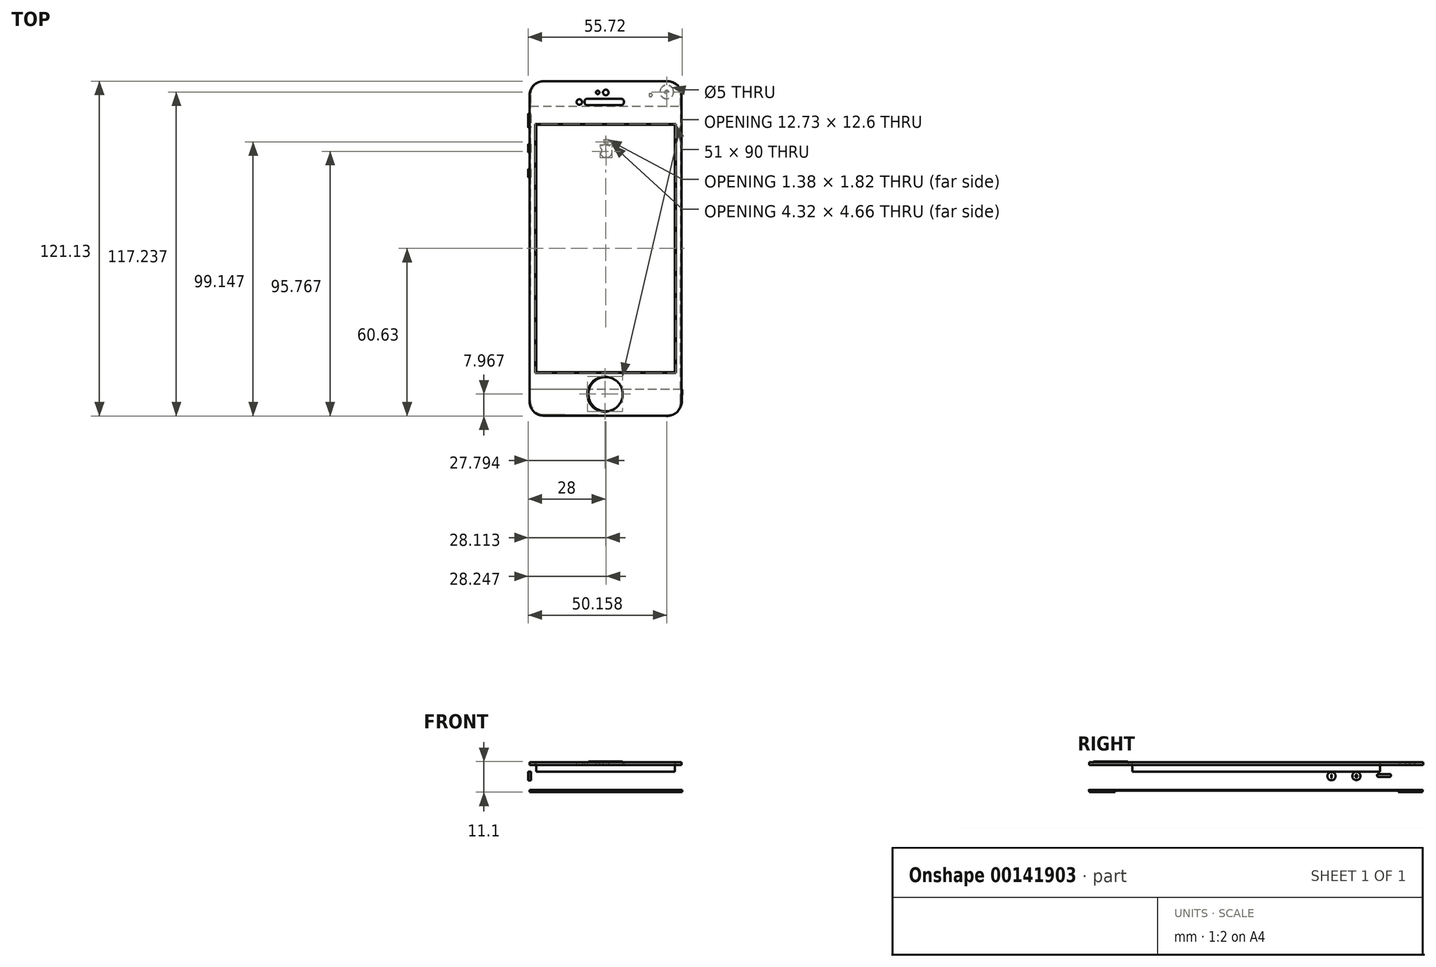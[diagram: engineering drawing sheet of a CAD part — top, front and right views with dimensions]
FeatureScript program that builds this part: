
annotation { "Feature Type Name" : "Feature", "Feature Type Description" : "" }
export const myFeature = defineFeature(function(context is Context, id is Id, definition is map)
    precondition{}
    {
        {
            assignVariable(context, id + "F0", {"name" : "depthofphone", "anyValue" : 1});
        }
        {
            var Q0;
            Q0=qCreatedBy(makeId("Top.planeOp"),FACE);
            var sketch = newSketch(context, id + "F1", { "sketchPlane" : qUnion([Q0])});
            skLineSegment(sketch, "E0.bottom", {"start": v(25.5, 45) * mm, "end": v(-25.5, 45) * mm});
            skLineSegment(sketch, "E0.top", {"start": v(25.5, -45) * mm, "end": v(-25.5, -45) * mm});
            skLineSegment(sketch, "E0.left", {"start": v(25.5, 45) * mm, "end": v(25.5, -45) * mm});
            skLineSegment(sketch, "E0.right", {"start": v(-25.5, 45) * mm, "end": v(-25.5, -45) * mm});
            skPoint(sketch, "E0.middle", {"position": v(0, 0) * mm});
            skLineSegment(sketch, "E1.bottom", {"start": v(22.5, 60.5) * mm, "end": v(-22.5, 60.5) * mm});
            skLineSegment(sketch, "E1.top", {"start": v(22.5, -60.5) * mm, "end": v(-22.5, -60.5) * mm});
            skLineSegment(sketch, "E1.left", {"start": v(27.5, 55.5) * mm, "end": v(27.5, -55.5) * mm});
            skLineSegment(sketch, "E1.right", {"start": v(-27.5, 55.5) * mm, "end": v(-27.5, -55.5) * mm});
            skPoint(sketch, "E2.visualSharp", {"position": v(-27.5, 60.5) * mm});
            skArc(sketch, "E2.filletArc", {"start": v(-22.5, 60.5) * mm, "mid": v(-26.04, 59.04) * mm, "end": v(-27.5, 55.5) * mm});
            skPoint(sketch, "E3.visualSharp", {"position": v(27.5, 60.5) * mm});
            skArc(sketch, "E3.filletArc", {"start": v(27.5, 55.5) * mm, "mid": v(26.04, 59.04) * mm, "end": v(22.5, 60.5) * mm});
            skPoint(sketch, "E4.visualSharp", {"position": v(-27.5, -60.5) * mm});
            skArc(sketch, "E4.filletArc", {"start": v(-27.5, -55.5) * mm, "mid": v(-26.04, -59.04) * mm, "end": v(-22.5, -60.5) * mm});
            skPoint(sketch, "E5.visualSharp", {"position": v(27.5, -60.5) * mm});
            skArc(sketch, "E5.filletArc", {"start": v(22.5, -60.5) * mm, "mid": v(26.04, -59.04) * mm, "end": v(27.5, -55.5) * mm});
            skSolve(sketch);
        }
        {
            var Q0;
            Q0=qCreatedBy(makeId("Top.planeOp"),FACE);
            cPlane(context, id + "F2", {"entities" : qUnion([Q0]), "cplaneType" : CPlaneType.OFFSET, "offset" : 2 * mm, "width" : 150 * mm, "height" : 150 * mm});
        }
        {
            var Q0;
            Q0=qCreatedBy(id+"F2.planeOp",FACE);
            var sketch = newSketch(context, id + "F3", { "sketchPlane" : qUnion([Q0])});
            skLineSegment(sketch, "E6", {"start": v(-6.75, 52) * mm, "end": v(5.75, 52) * mm});
            skLineSegment(sketch, "E7", {"start": v(6.5, 52.75) * mm, "end": v(6.5, 53.25) * mm});
            skLineSegment(sketch, "E8", {"start": v(5.75, 54) * mm, "end": v(-6.75, 54) * mm});
            skLineSegment(sketch, "E9", {"start": v(-7.5, 53.25) * mm, "end": v(-7.5, 52.75) * mm});
            skPoint(sketch, "E10.visualSharp", {"position": v(-7.5, 54) * mm});
            skArc(sketch, "E10.filletArc", {"start": v(-6.75, 54) * mm, "mid": v(-7.28, 53.78) * mm, "end": v(-7.5, 53.25) * mm});
            skPoint(sketch, "E11.visualSharp", {"position": v(-7.5, 52) * mm});
            skArc(sketch, "E11.filletArc", {"start": v(-7.5, 52.75) * mm, "mid": v(-7.28, 52.22) * mm, "end": v(-6.75, 52) * mm});
            skPoint(sketch, "E12.visualSharp", {"position": v(6.5, 52) * mm});
            skArc(sketch, "E12.filletArc", {"start": v(5.75, 52) * mm, "mid": v(6.28, 52.22) * mm, "end": v(6.5, 52.75) * mm});
            skPoint(sketch, "E13.visualSharp", {"position": v(6.5, 54) * mm});
            skArc(sketch, "E13.filletArc", {"start": v(6.5, 53.25) * mm, "mid": v(6.28, 53.78) * mm, "end": v(5.75, 54) * mm});
            skCircle(sketch, "E14", {"center": v(-9.5, 52.96) * mm, "radius": 0.9 * mm});
            skCircle(sketch, "E15", {"center": v(0.08, 56.42) * mm, "radius": 0.92 * mm});
            skCircle(sketch, "E16", {"center": v(-2.85, 56.45) * mm, "radius": 0.51 * mm});
            skCircle(sketch, "E17", {"center": v(-0.25, -52.75) * mm, "radius": 6.25 * mm});
            skSolve(sketch);
        }
        {
            var Q0;
            Q0 = qSketchRegion(id + "F1", true);
            extrude(context, id + "F4", {"entities" : qUnion([Q0]), "oppositeDirection" : true, "depth" : (getVariable(context, 'depthofphone')) * mm});
        }
        {
            var Q0;
            Q0 = qSketchRegion(id + "F3", true);
            extrude(context, id + "F5", {"entities" : qUnion([Q0]), "operationType" : NewBodyOperationType.REMOVE, "oppositeDirection" : true, "depth" : 3.74 * mm, "hasDraft" : true, "draftAngle" : 3 * degree});
        }
        {
            var Q0;
            Q0=qCreatedBy(makeId("Top.planeOp"),FACE);
            cPlane(context, id + "F6", {"entities" : qUnion([Q0]), "cplaneType" : CPlaneType.OFFSET, "offset" : 0.1 * mm, "oppositeDirection" : true, "width" : 150 * mm, "height" : 150 * mm});
        }
        {
            var Q0;
            Q0=qCreatedBy(id+"F6.planeOp",FACE);
            var sketch = newSketch(context, id + "F7", { "sketchPlane" : qUnion([Q0])});
            skLineSegment(sketch, "E18.bottom", {"start": v(25.05, 44.77) * mm, "end": v(-25.05, 44.77) * mm});
            skLineSegment(sketch, "E18.top", {"start": v(25.05, -44.77) * mm, "end": v(-25.05, -44.77) * mm});
            skLineSegment(sketch, "E18.left", {"start": v(25.05, 44.77) * mm, "end": v(25.05, -44.77) * mm});
            skLineSegment(sketch, "E18.right", {"start": v(-25.05, 44.77) * mm, "end": v(-25.05, -44.77) * mm});
            skPoint(sketch, "E18.middle", {"position": v(0, 0) * mm});
            skSolve(sketch);
        }
        {
            var Q0;
            Q0 = qSketchRegion(id + "F7", true);
            extrude(context, id + "F8", {"entities" : qUnion([Q0]), "oppositeDirection" : true, "depth" : 3.38 * mm});
        }
        {
            var Q0;
            Q0=qCreatedBy(id+"F6.planeOp",FACE);
            cPlane(context, id + "F9", {"entities" : qUnion([Q0]), "cplaneType" : CPlaneType.OFFSET, "offset" : 10 * mm, "oppositeDirection" : true, "width" : 150 * mm, "height" : 150 * mm});
        }
        {
            var Q0;
            Q0=qCreatedBy(id+"F9.planeOp",FACE);
            var sketch = newSketch(context, id + "F10", { "sketchPlane" : qUnion([Q0])});
            skLineSegment(sketch, "E19.left", {"start": v(27.13, -55.64) * mm, "end": v(27.22, 55.3) * mm});
            skLineSegment(sketch, "E19.right", {"start": v(-27.22, -55.1) * mm, "end": v(-27.13, 55.53) * mm});
            skPoint(sketch, "E19.middle", {"position": v(0, 0) * mm});
            skLineSegment(sketch, "E20", {"start": v(1.17, 33.01) * mm, "end": v(0.88, 32.83) * mm});
            skFitSpline(sketch, "E21", {"points": [v(-0.8, 33.02) * mm, v(-1.91, 34.28) * mm], "startDerivative": vector(-0.77, 0.53) * mm, "endDerivative": vector(-0.16, 0.9) * mm});
            skArc(sketch, "E22", {"start": v(1.17, 33.01) * mm, "mid": v(2.4, 35.13) * mm, "end": v(1.16, 37.25) * mm});
            skFitSpline(sketch, "E23", {"points": [v(1.16, 37.25) * mm, v(0.96, 37.34) * mm, v(0.74, 37.34) * mm, v(0.5, 37.25) * mm, v(0.3, 37.4) * mm, v(-0.28, 37.46) * mm, v(-1.27, 37.25) * mm, v(-1.91, 36.38) * mm], "startDerivative": vector(-2.14, 1.37) * mm, "endDerivative": vector(-2.3, -4.96) * mm});
            skFitSpline(sketch, "E24", {"points": [v(0.88, 32.83) * mm, v(0.59, 32.83) * mm, v(0.35, 33.06) * mm, v(-0.02, 33.08) * mm, v(-0.23, 32.83) * mm, v(-0.8, 33.02) * mm], "startDerivative": vector(-1.8, -0.36) * mm, "endDerivative": vector(-2.64, 1.48) * mm});
            skArc(sketch, "E25", {"start": v(-1.91, 36.38) * mm, "mid": v(-1.32, 35.33) * mm, "end": v(-1.91, 34.28) * mm});
            skFitSpline(sketch, "E26", {"points": [v(0.75, 37.6) * mm, v(-0.23, 38.24) * mm, v(-0.49, 39.44) * mm, v(0.49, 38.65) * mm, v(0.8, 37.99) * mm, v(0.75, 37.6) * mm]});
            skPoint(sketch, "E27.visualSharp", {"position": v(-27.22, -65.5) * mm});
            skPoint(sketch, "E28.visualSharp", {"position": v(27.12, -66.16) * mm});
            skPoint(sketch, "E29.visualSharp", {"position": v(-27.12, 66.16) * mm});
            skLineSegment(sketch, "E30", {"start": v(22.2, 60.3) * mm, "end": v(-22.42, 60.2) * mm});
            skLineSegment(sketch, "E31", {"start": v(22.07, -60.63) * mm, "end": v(-22.27, -60.1) * mm});
            skPoint(sketch, "E32.visualSharp", {"position": v(27.13, -60.7) * mm});
            skArc(sketch, "E32.filletArc", {"start": v(22.07, -60.63) * mm, "mid": v(25.65, -59.19) * mm, "end": v(27.13, -55.64) * mm});
            skPoint(sketch, "E33.visualSharp", {"position": v(-27.22, -60.05) * mm});
            skArc(sketch, "E33.filletArc", {"start": v(-27.22, -55.1) * mm, "mid": v(-25.77, -58.62) * mm, "end": v(-22.27, -60.1) * mm});
            skPoint(sketch, "E34.visualSharp", {"position": v(27.22, 60.3) * mm});
            skArc(sketch, "E34.filletArc", {"start": v(27.22, 55.3) * mm, "mid": v(25.75, 58.84) * mm, "end": v(22.2, 60.3) * mm});
            skPoint(sketch, "E35.visualSharp", {"position": v(-27.13, 60.2) * mm});
            skLineSegment(sketch, "E36", {"start": v(-25.9, 58.82) * mm, "end": v(-26.18, 58.5) * mm});
            skPoint(sketch, "E37.visualSharp", {"position": v(-27.13, 57.4) * mm});
            skArc(sketch, "E37.filletArc", {"start": v(-25.9, 58.82) * mm, "mid": v(-26.81, 57.29) * mm, "end": v(-27.13, 55.53) * mm});
            skPoint(sketch, "E38.visualSharp", {"position": v(-24.69, 60.2) * mm});
            skArc(sketch, "E38.filletArc", {"start": v(-22.42, 60.2) * mm, "mid": v(-24.49, 59.76) * mm, "end": v(-26.18, 58.5) * mm});
            skSolve(sketch);
        }
        {
            var Q0;
            Q0 = qSketchRegion(id + "F10", true);
            extrude(context, id + "F11", {"entities" : qUnion([Q0]), "oppositeDirection" : true, "depth" : 0.25 * mm});
        }
        {
            var Q0;
            Q0=qCreatedBy(id+"F9.planeOp",FACE);
            var sketch = newSketch(context, id + "F12", { "sketchPlane" : qUnion([Q0])});
            skLineSegment(sketch, "E39", {"start": v(-27.17, 51.46) * mm, "end": v(27.1, 51.46) * mm});
            skLineSegment(sketch, "E40", {"start": v(27.1, 51.46) * mm, "end": v(27.1, 55.4) * mm});
            skLineSegment(sketch, "E41", {"start": v(25.88, 58.7) * mm, "end": v(25.72, 58.87) * mm});
            skLineSegment(sketch, "E42", {"start": v(22.28, 60.23) * mm, "end": v(-22.4, 60.23) * mm});
            skLineSegment(sketch, "E43", {"start": v(-25.58, 59.1) * mm, "end": v(-25.85, 58.84) * mm});
            skLineSegment(sketch, "E44", {"start": v(-27.12, 55.56) * mm, "end": v(-27.17, 51.46) * mm});
            skPoint(sketch, "E45.visualSharp", {"position": v(-27.1, 57.66) * mm});
            skArc(sketch, "E45.filletArc", {"start": v(-25.58, 59.1) * mm, "mid": v(-26.7, 57.49) * mm, "end": v(-27.12, 55.56) * mm});
            skPoint(sketch, "E46.visualSharp", {"position": v(-24.4, 60.23) * mm});
            skArc(sketch, "E46.filletArc", {"start": v(-22.4, 60.23) * mm, "mid": v(-24.26, 59.87) * mm, "end": v(-25.85, 58.84) * mm});
            skPoint(sketch, "E47.visualSharp", {"position": v(24.4, 60.23) * mm});
            skArc(sketch, "E47.filletArc", {"start": v(25.88, 58.7) * mm, "mid": v(24.24, 59.83) * mm, "end": v(22.28, 60.23) * mm});
            skPoint(sketch, "E48.visualSharp", {"position": v(27.1, 57.41) * mm});
            skArc(sketch, "E48.filletArc", {"start": v(27.1, 55.4) * mm, "mid": v(26.75, 57.27) * mm, "end": v(25.72, 58.87) * mm});
            skCircle(sketch, "E49", {"center": v(22.16, 56.6) * mm, "radius": 2.5 * mm});
            skCircle(sketch, "E50", {"center": v(18.83, 56.45) * mm, "radius": 0.05 * mm});
            skLineSegment(sketch, "E51.bottom", {"start": v(16.08, 56.07) * mm, "end": v(16.46, 56.07) * mm});
            skLineSegment(sketch, "E51.top", {"start": v(16.08, 54.96) * mm, "end": v(16.46, 54.96) * mm});
            skLineSegment(sketch, "E51.left", {"start": v(15.77, 55.76) * mm, "end": v(15.77, 55.26) * mm});
            skLineSegment(sketch, "E51.right", {"start": v(16.77, 55.76) * mm, "end": v(16.77, 55.26) * mm});
            skPoint(sketch, "E51.middle", {"position": v(16.27, 55.51) * mm});
            skPoint(sketch, "E52.visualSharp", {"position": v(16.77, 56.07) * mm});
            skArc(sketch, "E52.filletArc", {"start": v(16.77, 55.76) * mm, "mid": v(16.68, 55.98) * mm, "end": v(16.46, 56.07) * mm});
            skPoint(sketch, "E53.visualSharp", {"position": v(15.77, 56.07) * mm});
            skArc(sketch, "E53.filletArc", {"start": v(16.08, 56.07) * mm, "mid": v(15.86, 55.98) * mm, "end": v(15.77, 55.76) * mm});
            skPoint(sketch, "E54.visualSharp", {"position": v(16.77, 54.96) * mm});
            skArc(sketch, "E54.filletArc", {"start": v(16.46, 54.96) * mm, "mid": v(16.68, 55.05) * mm, "end": v(16.77, 55.26) * mm});
            skPoint(sketch, "E55.visualSharp", {"position": v(15.77, 54.96) * mm});
            skArc(sketch, "E55.filletArc", {"start": v(15.77, 55.26) * mm, "mid": v(15.86, 55.05) * mm, "end": v(16.08, 54.96) * mm});
            skLineSegment(sketch, "E56", {"start": v(27.72, -51.08) * mm, "end": v(-27.5, -51.08) * mm});
            skLineSegment(sketch, "E57", {"start": v(-27.5, -51.08) * mm, "end": v(-27.5, -55.4) * mm});
            skLineSegment(sketch, "E58", {"start": v(-26.1, -58.85) * mm, "end": v(-26.1, -58.86) * mm});
            skLineSegment(sketch, "E59", {"start": v(-22.5, -60.4) * mm, "end": v(22.37, -60.4) * mm});
            skLineSegment(sketch, "E60", {"start": v(25.82, -59) * mm, "end": v(26.12, -58.72) * mm});
            skLineSegment(sketch, "E61", {"start": v(27.66, -55.17) * mm, "end": v(27.72, -51.08) * mm});
            skPoint(sketch, "E62.visualSharp", {"position": v(27.64, -57.27) * mm});
            skArc(sketch, "E62.filletArc", {"start": v(26.12, -58.72) * mm, "mid": v(27.25, -57.1) * mm, "end": v(27.66, -55.17) * mm});
            skPoint(sketch, "E63.visualSharp", {"position": v(24.37, -60.4) * mm});
            skArc(sketch, "E63.filletArc", {"start": v(22.37, -60.4) * mm, "mid": v(24.23, -60.03) * mm, "end": v(25.82, -59) * mm});
            skPoint(sketch, "E64.visualSharp", {"position": v(-24.62, -60.4) * mm});
            skArc(sketch, "E64.filletArc", {"start": v(-26.1, -58.86) * mm, "mid": v(-24.45, -60) * mm, "end": v(-22.5, -60.4) * mm});
            skPoint(sketch, "E65.visualSharp", {"position": v(-27.5, -57.4) * mm});
            skArc(sketch, "E65.filletArc", {"start": v(-27.5, -55.4) * mm, "mid": v(-27.13, -57.26) * mm, "end": v(-26.1, -58.85) * mm});
            skSolve(sketch);
        }
        {
            var Q0;
            Q0 = qSketchRegion(id + "F12", true);
            extrude(context, id + "F13", {"entities" : qUnion([Q0]), "oppositeDirection" : true, "depth" : 0.75 * mm});
        }
        {
            var Q0;
            Q0=qCreatedBy(id+"F9.planeOp",FACE);
            var sketch = newSketch(context, id + "F14", { "sketchPlane" : qUnion([Q0])});
            skCircle(sketch, "E66", {"center": v(22.16, 56.46) * mm, "radius": 0.74 * mm});
            skSolve(sketch);
        }
        {
            var Q0;
            Q0 = qSketchRegion(id + "F14", true);
            extrude(context, id + "F15", {"entities" : qUnion([Q0]), "oppositeDirection" : true, "depth" : 0.65 * mm});
        }
        {
            var Q0;
            Q0=qCreatedBy(id+"F9.planeOp",FACE);
            var sketch = newSketch(context, id + "F16", { "sketchPlane" : qUnion([Q0])});
            skCircle(sketch, "E67", {"center": v(22.15, 56.61) * mm, "radius": 2.42 * mm});
            skSolve(sketch);
        }
        {
            var Q0;
            Q0 = qSketchRegion(id + "F16", true);
            extrude(context, id + "F17", {"entities" : qUnion([Q0]), "oppositeDirection" : true, "depth" : 0.6 * mm});
        }
        {
            var Q0;
            Q0=qCreatedBy(id+"F9.planeOp",FACE);
            var sketch = newSketch(context, id + "F18", { "sketchPlane" : qUnion([Q0])});
            skLineSegment(sketch, "E68.bottom", {"start": v(16.07, 56.06) * mm, "end": v(16.45, 56.06) * mm});
            skLineSegment(sketch, "E68.top", {"start": v(16.07, 54.95) * mm, "end": v(16.45, 54.95) * mm});
            skLineSegment(sketch, "E68.left", {"start": v(15.76, 55.75) * mm, "end": v(15.76, 55.25) * mm});
            skLineSegment(sketch, "E68.right", {"start": v(16.75, 55.75) * mm, "end": v(16.75, 55.25) * mm});
            skPoint(sketch, "E68.middle", {"position": v(16.26, 55.5) * mm});
            skPoint(sketch, "E69.visualSharp", {"position": v(16.75, 56.06) * mm});
            skArc(sketch, "E69.filletArc", {"start": v(16.75, 55.75) * mm, "mid": v(16.66, 55.97) * mm, "end": v(16.45, 56.06) * mm});
            skPoint(sketch, "E70.visualSharp", {"position": v(15.76, 56.06) * mm});
            skArc(sketch, "E70.filletArc", {"start": v(16.07, 56.06) * mm, "mid": v(15.85, 55.97) * mm, "end": v(15.76, 55.75) * mm});
            skPoint(sketch, "E71.visualSharp", {"position": v(16.75, 54.95) * mm});
            skArc(sketch, "E71.filletArc", {"start": v(16.45, 54.95) * mm, "mid": v(16.66, 55.04) * mm, "end": v(16.75, 55.25) * mm});
            skPoint(sketch, "E72.visualSharp", {"position": v(15.76, 54.95) * mm});
            skArc(sketch, "E72.filletArc", {"start": v(15.76, 55.25) * mm, "mid": v(15.85, 55.04) * mm, "end": v(16.07, 54.95) * mm});
            skSolve(sketch);
        }
        {
            var Q0;
            Q0 = qSketchRegion(id + "F18", true);
            extrude(context, id + "F19", {"entities" : qUnion([Q0]), "oppositeDirection" : true, "depth" : 0.72 * mm});
        }
        {
            var Q0;
            Q0=qCreatedBy(makeId("Top.planeOp"),FACE);
            var sketch = newSketch(context, id + "F20", { "sketchPlane" : qUnion([Q0])});
            skCircle(sketch, "E73", {"center": v(0, -52.72) * mm, "radius": 6.2 * mm});
            skSolve(sketch);
        }
        {
            var Q0;
            Q0 = qSketchRegion(id + "F20", true);
            extrude(context, id + "F21", {"entities" : qUnion([Q0]), "operationType" : NewBodyOperationType.ADD, "depth" : 0.25 * mm});
        }
        {
            var Q0;
            Q0=qCreatedBy(makeId("Right.planeOp"),FACE);
            cPlane(context, id + "F22", {"entities" : qUnion([Q0]), "cplaneType" : CPlaneType.OFFSET, "offset" : 27 * mm, "width" : 150 * mm, "height" : 150 * mm});
        }
        {
            var Q0;
            Q0=qCreatedBy(makeId("Front.planeOp"),FACE);
            cPlane(context, id + "F23", {"entities" : qUnion([Q0]), "cplaneType" : CPlaneType.OFFSET, "offset" : 60.65 * mm, "width" : 150 * mm, "height" : 150 * mm});
        }
        {
            var Q0;
            Q0=qCreatedBy(makeId("Right.planeOp"),FACE);
            cPlane(context, id + "F24", {"entities" : qUnion([Q0]), "cplaneType" : CPlaneType.OFFSET, "offset" : 27 * mm, "oppositeDirection" : true, "width" : 150 * mm, "height" : 150 * mm});
        }
        {
            var Q0;
            Q0=qCreatedBy(id+"F24.planeOp",FACE);
            var sketch = newSketch(context, id + "F25", { "sketchPlane" : qUnion([Q0])});
            skLineSegment(sketch, "E74", {"start": v(48.36, -4.3) * mm, "end": v(44.13, -4.3) * mm});
            skLineSegment(sketch, "E75", {"start": v(48.74, -4.69) * mm, "end": v(48.74, -4.92) * mm});
            skLineSegment(sketch, "E76", {"start": v(48.36, -5.3) * mm, "end": v(44.14, -5.3) * mm});
            skLineSegment(sketch, "E77", {"start": v(43.76, -4.93) * mm, "end": v(43.75, -4.7) * mm});
            skArc(sketch, "E78.filletArc", {"start": v(48.74, -4.69) * mm, "mid": v(48.63, -4.42) * mm, "end": v(48.36, -4.3) * mm});
            skPoint(sketch, "E79.visualSharp", {"position": v(48.74, -5.3) * mm});
            skArc(sketch, "E79.filletArc", {"start": v(48.36, -5.3) * mm, "mid": v(48.63, -5.2) * mm, "end": v(48.74, -4.92) * mm});
            skPoint(sketch, "E80.visualSharp", {"position": v(43.77, -5.3) * mm});
            skArc(sketch, "E80.filletArc", {"start": v(43.76, -4.93) * mm, "mid": v(43.87, -5.2) * mm, "end": v(44.14, -5.3) * mm});
            skPoint(sketch, "E81.visualSharp", {"position": v(43.74, -4.3) * mm});
            skArc(sketch, "E81.filletArc", {"start": v(44.13, -4.3) * mm, "mid": v(43.86, -4.42) * mm, "end": v(43.75, -4.7) * mm});
            skCircle(sketch, "E82", {"center": v(36.26, -4.99) * mm, "radius": 1.5 * mm});
            skCircle(sketch, "E83", {"center": v(27.26, -5.06) * mm, "radius": 1.5 * mm});
            skLineSegment(sketch, "E84.bottom", {"start": v(27.31, -4.44) * mm, "end": v(27.2, -4.44) * mm});
            skLineSegment(sketch, "E84.top", {"start": v(27.31, -5.68) * mm, "end": v(27.2, -5.68) * mm});
            skLineSegment(sketch, "E84.left", {"start": v(27.31, -4.44) * mm, "end": v(27.31, -5.68) * mm});
            skLineSegment(sketch, "E84.right", {"start": v(27.2, -4.44) * mm, "end": v(27.2, -5.68) * mm});
            skLineSegment(sketch, "E85.bottom", {"start": v(36.32, -4.3) * mm, "end": v(36.2, -4.3) * mm});
            skLineSegment(sketch, "E85.top", {"start": v(36.32, -5.67) * mm, "end": v(36.2, -5.67) * mm});
            skLineSegment(sketch, "E85.left", {"start": v(36.32, -4.3) * mm, "end": v(36.32, -5.67) * mm});
            skLineSegment(sketch, "E85.right", {"start": v(36.2, -4.3) * mm, "end": v(36.2, -5.67) * mm});
            skLineSegment(sketch, "E86.bottom", {"start": v(36.8, -5.04) * mm, "end": v(35.72, -5.04) * mm});
            skLineSegment(sketch, "E86.top", {"start": v(36.8, -4.93) * mm, "end": v(35.72, -4.93) * mm});
            skLineSegment(sketch, "E86.left", {"start": v(36.8, -5.04) * mm, "end": v(36.8, -4.93) * mm});
            skLineSegment(sketch, "E86.right", {"start": v(35.72, -5.04) * mm, "end": v(35.72, -4.93) * mm});
            skSolve(sketch);
        }
        {
            var Q0;
            Q0 = qSketchRegion(id + "F25", true);
            extrude(context, id + "F26", {"entities" : qUnion([Q0]), "operationType" : NewBodyOperationType.ADD, "oppositeDirection" : true, "depth" : 1 * mm});
        }
        {
            var Q0;
            Q0=qCreatedBy(id+"F23.planeOp",FACE);
            var sketch = newSketch(context, id + "F27", { "sketchPlane" : qUnion([Q0])});
            skCircle(sketch, "E87", {"center": v(22.28, -6.33) * mm, "radius": 0.45 * mm});
            skLineSegment(sketch, "E88.bottom", {"start": v(3.72, -6.28) * mm, "end": v(-3.72, -6.28) * mm});
            skLineSegment(sketch, "E88.top", {"start": v(3.72, -4.12) * mm, "end": v(-3.72, -4.12) * mm});
            skLineSegment(sketch, "E88.left", {"start": v(4.1, -5.9) * mm, "end": v(4.1, -4.5) * mm});
            skLineSegment(sketch, "E88.right", {"start": v(-4.1, -5.9) * mm, "end": v(-4.1, -4.5) * mm});
            skPoint(sketch, "E88.middle", {"position": v(0, -5.2) * mm});
            skPoint(sketch, "E89.visualSharp", {"position": v(-4.1, -4.12) * mm});
            skArc(sketch, "E89.filletArc", {"start": v(-3.72, -4.12) * mm, "mid": v(-4, -4.23) * mm, "end": v(-4.1, -4.5) * mm});
            skPoint(sketch, "E90.visualSharp", {"position": v(-4.1, -6.28) * mm});
            skArc(sketch, "E90.filletArc", {"start": v(-4.1, -5.9) * mm, "mid": v(-4, -6.17) * mm, "end": v(-3.72, -6.28) * mm});
            skPoint(sketch, "E91.visualSharp", {"position": v(4.1, -6.28) * mm});
            skArc(sketch, "E91.filletArc", {"start": v(3.72, -6.28) * mm, "mid": v(4, -6.17) * mm, "end": v(4.1, -5.9) * mm});
            skPoint(sketch, "E92.visualSharp", {"position": v(4.1, -4.12) * mm});
            skArc(sketch, "E92.filletArc", {"start": v(4.1, -4.5) * mm, "mid": v(4, -4.23) * mm, "end": v(3.72, -4.12) * mm});
            skCircle(sketch, "E93.1.0.0", {"center": v(20.78, -6.33) * mm, "radius": 0.45 * mm});
            skCircle(sketch, "E93.2.0.0", {"center": v(19.28, -6.33) * mm, "radius": 0.45 * mm});
            skCircle(sketch, "E93.3.0.0", {"center": v(17.78, -6.33) * mm, "radius": 0.45 * mm});
            skCircle(sketch, "E93.4.0.0", {"center": v(16.28, -6.33) * mm, "radius": 0.45 * mm});
            skLineSegment(sketch, "E93.direction1", {"start": v(22.28, -6.33) * mm, "end": v(20.78, -6.33) * mm, "construction": true});
            skCircle(sketch, "E94.0.5.0", {"center": v(14.78, -6.33) * mm, "radius": 0.45 * mm});
            skCircle(sketch, "E94.0.6.0", {"center": v(13.28, -6.33) * mm, "radius": 0.45 * mm});
            skCircle(sketch, "E94.0.7.0", {"center": v(11.78, -6.33) * mm, "radius": 0.45 * mm});
            skCircle(sketch, "E95", {"center": v(22.29, -4.83) * mm, "radius": 0.45 * mm});
            skCircle(sketch, "E96.1.0.0", {"center": v(20.79, -4.83) * mm, "radius": 0.45 * mm});
            skCircle(sketch, "E96.2.0.0", {"center": v(19.29, -4.83) * mm, "radius": 0.45 * mm});
            skCircle(sketch, "E96.3.0.0", {"center": v(17.79, -4.83) * mm, "radius": 0.45 * mm});
            skCircle(sketch, "E96.4.0.0", {"center": v(16.29, -4.83) * mm, "radius": 0.45 * mm});
            skCircle(sketch, "E96.5.0.0", {"center": v(14.79, -4.83) * mm, "radius": 0.45 * mm});
            skCircle(sketch, "E96.6.0.0", {"center": v(13.29, -4.83) * mm, "radius": 0.45 * mm});
            skCircle(sketch, "E96.7.0.0", {"center": v(11.79, -4.83) * mm, "radius": 0.45 * mm});
            skLineSegment(sketch, "E96.direction1", {"start": v(22.29, -4.83) * mm, "end": v(20.79, -4.83) * mm, "construction": true});
            skCircle(sketch, "E97", {"center": v(-20.1, -5.12) * mm, "radius": 2 * mm});
            skCircle(sketch, "E98", {"center": v(-16.05, -4.45) * mm, "radius": 0.45 * mm});
            skCircle(sketch, "E99.1.0.0", {"center": v(-14.55, -4.45) * mm, "radius": 0.45 * mm});
            skCircle(sketch, "E99.2.0.0", {"center": v(-13.05, -4.45) * mm, "radius": 0.45 * mm});
            skCircle(sketch, "E99.3.0.0", {"center": v(-11.55, -4.45) * mm, "radius": 0.45 * mm});
            skCircle(sketch, "E99.4.0.0", {"center": v(-10.05, -4.45) * mm, "radius": 0.45 * mm});
            skLineSegment(sketch, "E99.direction1", {"start": v(-16.05, -4.45) * mm, "end": v(-14.55, -4.45) * mm, "construction": true});
            skCircle(sketch, "E100", {"center": v(-16.03, -5.95) * mm, "radius": 0.45 * mm});
            skCircle(sketch, "E101.1.0.0", {"center": v(-14.53, -5.95) * mm, "radius": 0.45 * mm});
            skCircle(sketch, "E101.2.0.0", {"center": v(-13.03, -5.95) * mm, "radius": 0.45 * mm});
            skCircle(sketch, "E101.3.0.0", {"center": v(-11.53, -5.95) * mm, "radius": 0.45 * mm});
            skCircle(sketch, "E101.4.0.0", {"center": v(-10.03, -5.95) * mm, "radius": 0.45 * mm});
            skLineSegment(sketch, "E101.direction1", {"start": v(-16.03, -5.95) * mm, "end": v(-14.53, -5.95) * mm, "construction": true});
            skCircle(sketch, "E102", {"center": v(-7.18, -5.1) * mm, "radius": 0.7 * mm});
            skLineSegment(sketch, "E103.bottom", {"start": v(-7.13, -4.87) * mm, "end": v(-7.23, -4.87) * mm});
            skLineSegment(sketch, "E103.top", {"start": v(-7.13, -5.35) * mm, "end": v(-7.23, -5.35) * mm});
            skLineSegment(sketch, "E103.left", {"start": v(-7.13, -4.87) * mm, "end": v(-7.13, -5.35) * mm});
            skLineSegment(sketch, "E103.right", {"start": v(-7.23, -4.87) * mm, "end": v(-7.23, -5.35) * mm});
            skLineSegment(sketch, "E104.bottom", {"start": v(-6.96, -5.06) * mm, "end": v(-7.4, -5.06) * mm});
            skLineSegment(sketch, "E104.top", {"start": v(-6.96, -5.16) * mm, "end": v(-7.4, -5.16) * mm});
            skLineSegment(sketch, "E104.left", {"start": v(-6.96, -5.06) * mm, "end": v(-6.96, -5.16) * mm});
            skLineSegment(sketch, "E104.right", {"start": v(-7.4, -5.06) * mm, "end": v(-7.4, -5.16) * mm});
            skLineSegment(sketch, "E105.bottom", {"start": v(-7, -5.24) * mm, "end": v(-7.08, -5.3) * mm});
            skLineSegment(sketch, "E105.top", {"start": v(-7.27, -4.91) * mm, "end": v(-7.35, -4.98) * mm});
            skLineSegment(sketch, "E105.left", {"start": v(-7, -5.24) * mm, "end": v(-7.27, -4.91) * mm});
            skLineSegment(sketch, "E105.right", {"start": v(-7.08, -5.3) * mm, "end": v(-7.35, -4.98) * mm});
            skLineSegment(sketch, "E106.bottom", {"start": v(-7, -4.97) * mm, "end": v(-7.09, -4.9) * mm});
            skLineSegment(sketch, "E106.top", {"start": v(-7.27, -5.3) * mm, "end": v(-7.35, -5.25) * mm});
            skLineSegment(sketch, "E106.left", {"start": v(-7, -4.97) * mm, "end": v(-7.27, -5.3) * mm});
            skLineSegment(sketch, "E106.right", {"start": v(-7.09, -4.9) * mm, "end": v(-7.35, -5.25) * mm});
            skPoint(sketch, "E107.1.0.0", {"position": v(7.52, -5.1) * mm});
            skCircle(sketch, "E107.1.0.1", {"center": v(7.52, -5.1) * mm, "radius": 0.7 * mm});
            skPoint(sketch, "E107.1.0.2", {"position": v(7.52, -5.1) * mm});
            skLineSegment(sketch, "E107.1.0.3", {"start": v(7.74, -5.06) * mm, "end": v(7.74, -5.16) * mm});
            skLineSegment(sketch, "E107.1.0.4", {"start": v(7.47, -4.87) * mm, "end": v(7.47, -5.35) * mm});
            skLineSegment(sketch, "E107.1.0.5", {"start": v(7.7, -5.24) * mm, "end": v(7.62, -5.3) * mm});
            skLineSegment(sketch, "E107.1.0.6", {"start": v(7.43, -5.3) * mm, "end": v(7.35, -5.25) * mm});
            skLineSegment(sketch, "E107.1.0.7", {"start": v(7.57, -5.35) * mm, "end": v(7.47, -5.35) * mm});
            skLineSegment(sketch, "E107.1.0.8", {"start": v(7.61, -4.9) * mm, "end": v(7.35, -5.25) * mm});
            skPoint(sketch, "E107.1.0.9", {"position": v(7.52, -5.1) * mm});
            skLineSegment(sketch, "E107.1.0.10", {"start": v(7.57, -4.87) * mm, "end": v(7.57, -5.35) * mm});
            skLineSegment(sketch, "E107.1.0.11", {"start": v(7.7, -4.97) * mm, "end": v(7.61, -4.9) * mm});
            skLineSegment(sketch, "E107.1.0.12", {"start": v(7.3, -5.06) * mm, "end": v(7.3, -5.16) * mm});
            skLineSegment(sketch, "E107.1.0.13", {"start": v(7.74, -5.16) * mm, "end": v(7.3, -5.16) * mm});
            skLineSegment(sketch, "E107.1.0.14", {"start": v(7.57, -4.87) * mm, "end": v(7.47, -4.87) * mm});
            skLineSegment(sketch, "E107.1.0.15", {"start": v(7.62, -5.3) * mm, "end": v(7.35, -4.98) * mm});
            skLineSegment(sketch, "E107.1.0.16", {"start": v(7.43, -4.91) * mm, "end": v(7.35, -4.98) * mm});
            skLineSegment(sketch, "E107.1.0.17", {"start": v(7.7, -4.97) * mm, "end": v(7.43, -5.3) * mm});
            skLineSegment(sketch, "E107.1.0.18", {"start": v(7.74, -5.06) * mm, "end": v(7.3, -5.06) * mm});
            skLineSegment(sketch, "E107.1.0.19", {"start": v(7.7, -5.24) * mm, "end": v(7.43, -4.91) * mm});
            skPoint(sketch, "E107.1.0.20", {"position": v(7.52, -5.1) * mm});
            skLineSegment(sketch, "E107.direction1", {"start": v(-7.35, -5.25) * mm, "end": v(7.35, -5.25) * mm, "construction": true});
            skSolve(sketch);
        }
        {
            var Q0;
            Q0 = qSketchRegion(id + "F27", true);
            extrude(context, id + "F28", {"entities" : qUnion([Q0]), "operationType" : NewBodyOperationType.REMOVE, "oppositeDirection" : true, "depth" : 3 * mm});
        }
    });
